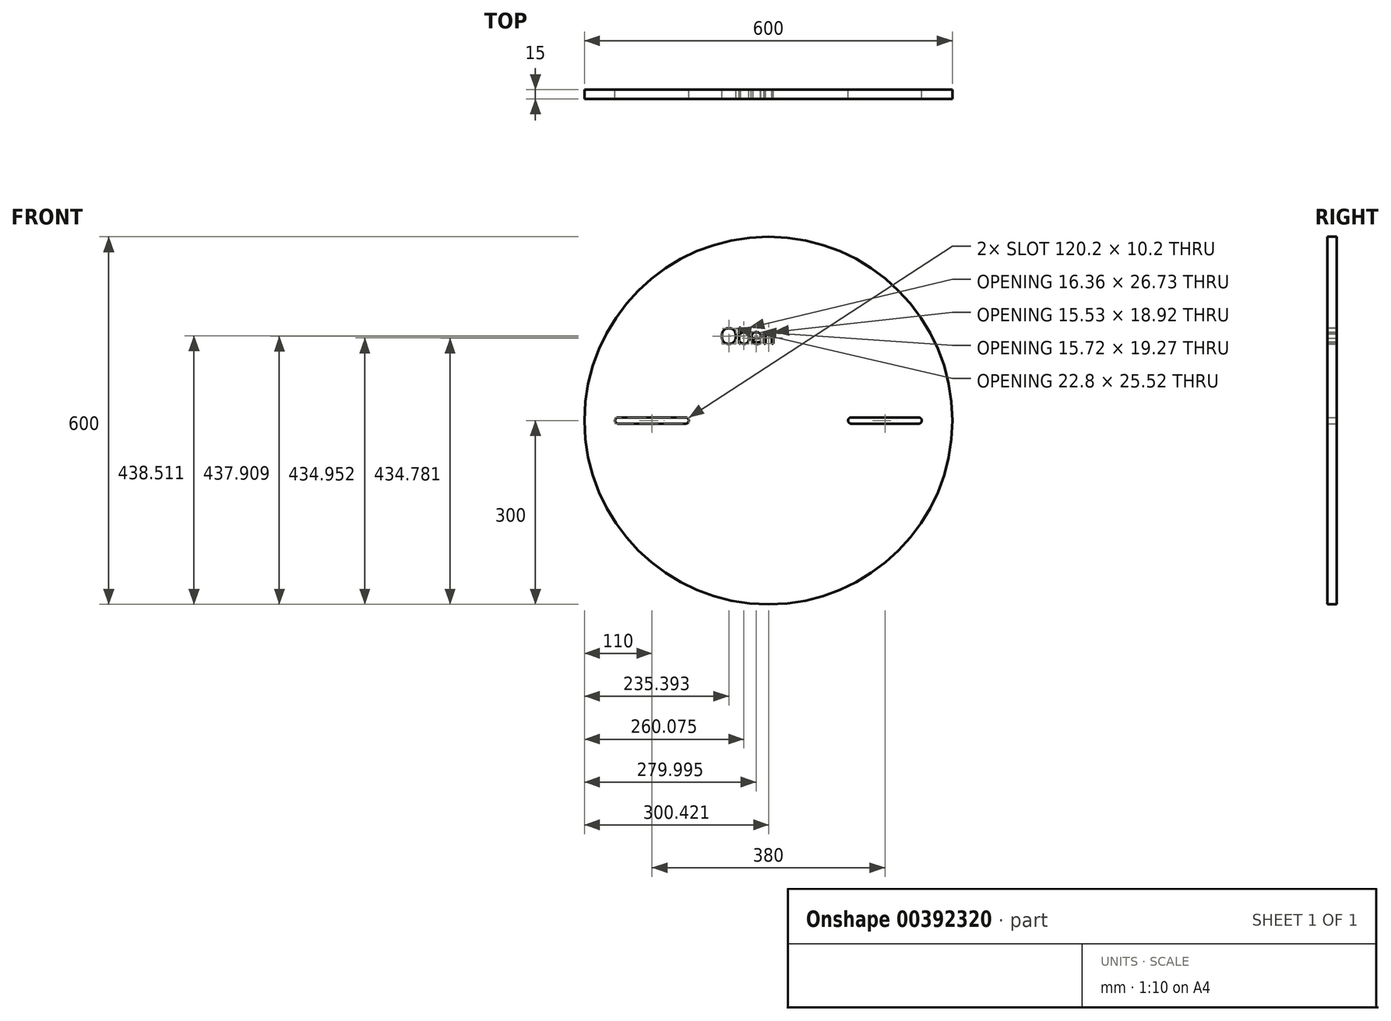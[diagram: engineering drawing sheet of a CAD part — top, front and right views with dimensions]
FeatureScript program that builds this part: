
annotation { "Feature Type Name" : "Feature", "Feature Type Description" : "" }
export const myFeature = defineFeature(function(context is Context, id is Id, definition is map)
    precondition{}
    {
        {
            var Q0;
            Q0=qCreatedBy(makeId("Front.planeOp"),FACE);
            var sketch = newSketch(context, id + "F0", { "sketchPlane" : qUnion([Q0])});
            skCircle(sketch, "E0", {"center": v(0, 0) * mm, "radius": 300 * mm});
            skLineSegment(sketch, "E1", {"start": v(-300, 0) * mm, "end": v(300, 0) * mm, "construction": true});
            skLineSegment(sketch, "E2.0", {"start": v(-245, 300) * mm, "end": v(-245, -300) * mm, "construction": true});
            skLineSegment(sketch, "E3.0", {"start": v(245, 300) * mm, "end": v(245, -300) * mm, "construction": true});
            skArc(sketch, "E4", {"start": v(-245, 5.1) * mm, "mid": v(-250.1, 0) * mm, "end": v(-245, -5.1) * mm});
            skLineSegment(sketch, "E5.0", {"start": v(145, 300) * mm, "end": v(145, -300) * mm, "construction": true});
            skArc(sketch, "E6", {"start": v(-135, -5.1) * mm, "mid": v(-129.9, 0) * mm, "end": v(-135, 5.1) * mm});
            skLineSegment(sketch, "E7", {"start": v(-245, -5.1) * mm, "end": v(-135, -5.1) * mm});
            skLineSegment(sketch, "E8", {"start": v(-245, 5.1) * mm, "end": v(-135, 5.1) * mm});
            skArc(sketch, "E9", {"start": v(134.97, 5.1) * mm, "mid": v(129.9, -0.03) * mm, "end": v(135.03, -5.1) * mm});
            skArc(sketch, "E10", {"start": v(245, -5.1) * mm, "mid": v(250.1, 0) * mm, "end": v(245, 5.1) * mm});
            skLineSegment(sketch, "E11", {"start": v(135.03, -5.1) * mm, "end": v(245, -5.1) * mm});
            skLineSegment(sketch, "E12", {"start": v(134.97, 5.1) * mm, "end": v(245, 5.1) * mm});
            skText(sketch, "E13", { "text": "Oben", "fontName": "OpenSans-Regular.ttf"});
            skLineSegment(sketch, "E14", {"start": v(0, 300) * mm, "end": v(0, -300) * mm, "construction": true});
            const initialGuessF0  = {"E13": [-0.07813, 0.12549, 1, 0, 0.025]};
            skSetInitialGuess(sketch, initialGuessF0);
            skSolve(sketch);
        }
        {
            var Q0;
            Q0 = qSketchRegion(id + "F0", true);
            extrude(context, id + "F1", {"entities" : qUnion([Q0]), "depth" : 15 * mm});
        }
    });
